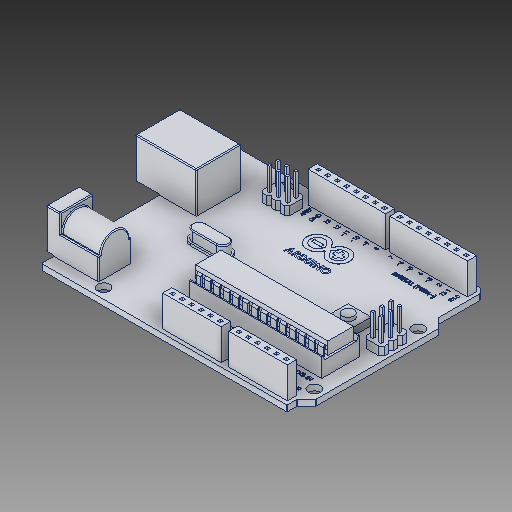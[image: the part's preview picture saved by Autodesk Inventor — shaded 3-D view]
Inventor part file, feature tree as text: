
AUTODESK INVENTOR PART (.ipt)
format: ipt  version: 2019 (Build 230136000, 136)  size: 2,956,800 bytes
history: mixed  units: mm
features: other x1, extrude x1, imported_body x1
ambient origin geometry x8: Origin, YZ Plane, XZ Plane, XY Plane, X Axis, Y Axis, Z Axis, Center Point
bodies: Body1 (imported_parasolid)
feature tree (3):
  other  "Твердое тело1"
  extrude  "Extrude19"  [1 undecoded]
  imported_body  NMx_Import_Brep_tag  [imported B-rep: ~50 faces, bbox_mm=[66.04, 7.3025, 53.34]]
note: 1 required parameter value undecoded (feature->parameter linkage not recoverable at this tier; creation-order binding heuristic only, values carry confidence <= 0.55)
